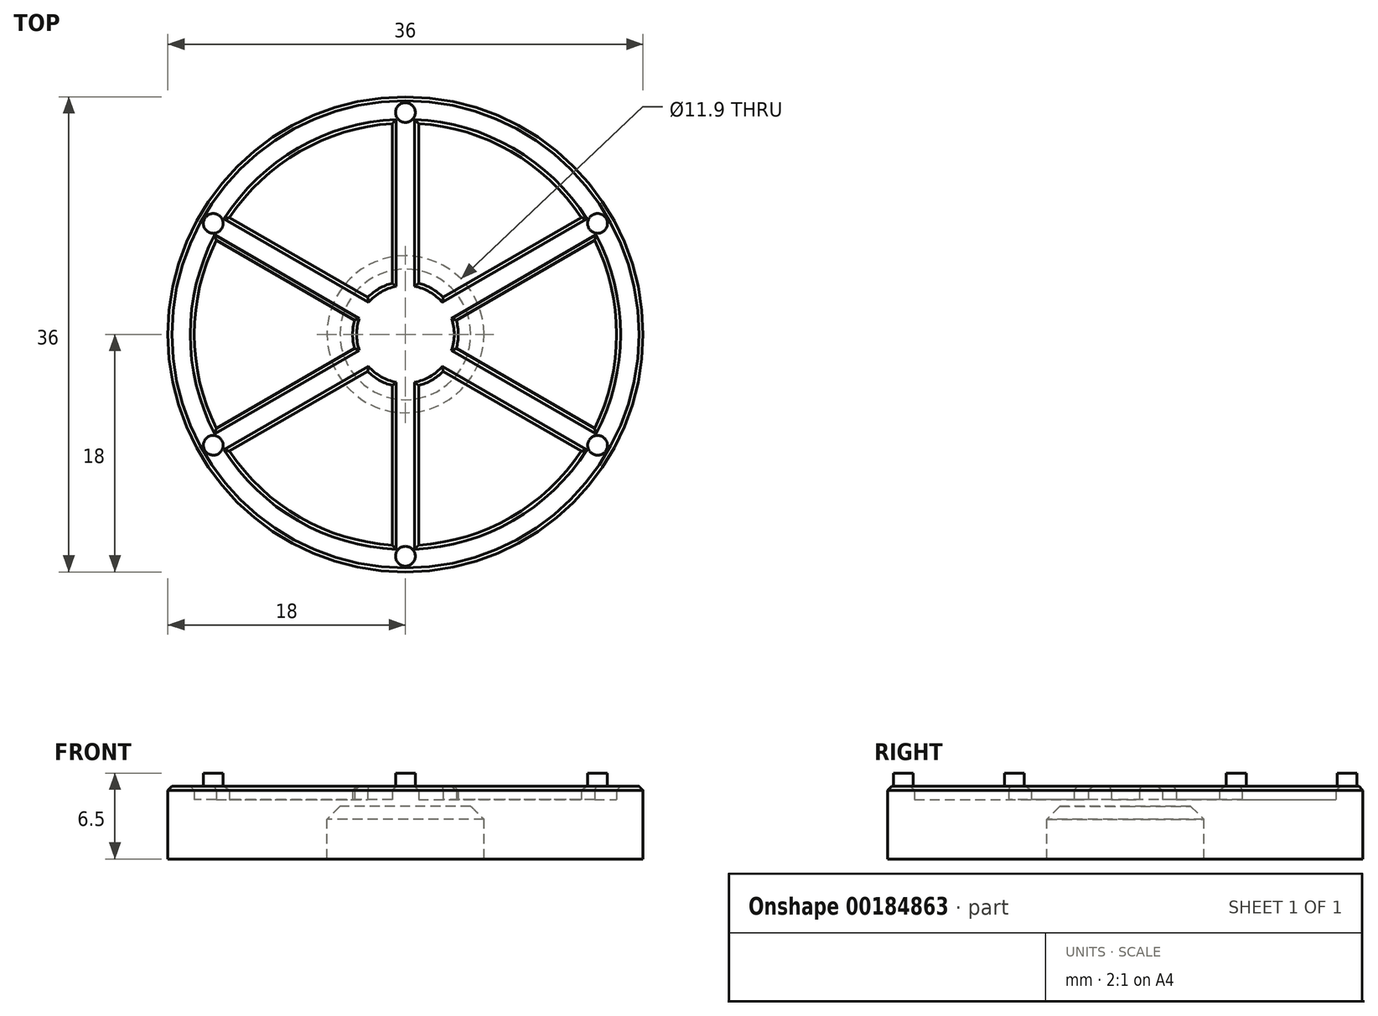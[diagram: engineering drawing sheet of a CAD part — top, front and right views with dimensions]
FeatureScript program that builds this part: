
annotation { "Feature Type Name" : "Feature", "Feature Type Description" : "" }
export const myFeature = defineFeature(function(context is Context, id is Id, definition is map)
    precondition{}
    {
        {
            var Q0;
            Q0=qCreatedBy(makeId("Top.planeOp"),FACE);
            var sketch = newSketch(context, id + "F0", { "sketchPlane" : qUnion([Q0])});
            skCircle(sketch, "E0", {"center": v(0, 0) * mm, "radius": 5.95 * mm});
            skCircle(sketch, "E1", {"center": v(0, 0) * mm, "radius": 18 * mm});
            skSolve(sketch);
        }
        {
            var Q0;
            Q0 = qSketchRegion(id + "F0", true);
            extrude(context, id + "F1", {"entities" : qUnion([Q0]), "oppositeDirection" : true, "depth" : 4 * mm});
        }
        {
            var Q0;
            Q0=qCreatedBy(makeId("Top.planeOp"),FACE);
            var sketch = newSketch(context, id + "F2", { "sketchPlane" : qUnion([Q0])});
            skCircle(sketch, "E2", {"center": v(0, 0) * mm, "radius": 18 * mm});
            skCircle(sketch, "E3", {"center": v(0, 0) * mm, "radius": 16 * mm});
            skSolve(sketch);
        }
        {
            var Q0;
            Q0 = qSketchRegion(id + "F2", true);
            extrude(context, id + "F3", {"entities" : qUnion([Q0]), "operationType" : NewBodyOperationType.ADD, "depth" : 1.5 * mm});
        }
        {
            var Q0;
            Q0=qCreatedBy(makeId("Top.planeOp"),FACE);
            var sketch = newSketch(context, id + "F4", { "sketchPlane" : qUnion([Q0])});
            skLineSegment(sketch, "E4.bottom", {"start": v(1, -16.78) * mm, "end": v(-1, -16.78) * mm});
            skLineSegment(sketch, "E4.top", {"start": v(1, 16.78) * mm, "end": v(-1, 16.78) * mm});
            skLineSegment(sketch, "E4.left", {"start": v(1, -16.78) * mm, "end": v(1, 16.78) * mm});
            skLineSegment(sketch, "E4.right", {"start": v(-1, -16.78) * mm, "end": v(-1, 16.78) * mm});
            skPoint(sketch, "E4.middle", {"position": v(0, 0) * mm});
            skCircle(sketch, "E5", {"center": v(0, 0) * mm, "radius": 4 * mm});
            skSolve(sketch);
        }
        {
            var Q0;
            Q0 = qSketchRegion(id + "F4", true);
            extrude(context, id + "F5", {"entities" : qUnion([Q0]), "depth" : 1.5 * mm});
        }
        {
            var Q0;
            {var subQ0=makeQuery(id+"F5.opExtrude","CAP_FACE",FACE,{"disambiguationData":[OSD([sQuery(id+"F4.wireOp",EDGE,"E4.bottom"),sQuery(id+"F4.wireOp",EDGE,"E4.top"),sQuery(id+"F4.wireOp",EDGE,"E4.left"),sQuery(id+"F4.wireOp",EDGE,"E4.right"),sQuery(id+"F4.wireOp",EDGE,"E5")])],"isStart":false});Q0=makeQuery(id+"F7.boolean.opBoolean","MERGE",FACE,{"derivedFrom":[makeQuery(id+"F3.opExtrude","CAP_FACE",FACE,{"disambiguationData":[OSD([sQuery(id+"F2.wireOp",EDGE,"E2"),sQuery(id+"F2.wireOp",EDGE,"E3")])],"isStart":false}),subQ0,makeQuery(id+"F7.opPattern","COPY",FACE,{"derivedFrom":subQ0,"instanceName":"1"}),makeQuery(id+"F7.opPattern","COPY",FACE,{"derivedFrom":subQ0,"instanceName":"2"})]});}
            chamfer(context, id + "F6", {"entities" : qUnion([Q0]), "width" : .3 * mm, "tangentPropagation" : true});
        }
        {
            var Q0;
            Q0=makeQuery(id+"F5.opExtrude","SWEPT_BODY",BODY,{"disambiguationData":[OSD([sQuery(id+"F4.wireOp",EDGE,"E4.bottom"),sQuery(id+"F4.wireOp",EDGE,"E4.top"),sQuery(id+"F4.wireOp",EDGE,"E4.left"),sQuery(id+"F4.wireOp",EDGE,"E4.right")])]});
            var Q1;
            Q1=makeQuery(id+"F1.opExtrude","CAP_EDGE",EDGE,{"disambiguationData":[OSD([sQuery(id+"F0.wireOp",EDGE,"E0")])],"isStart":true});
            circularPattern(context, id + "F7", {"operationType" : NewBodyOperationType.ADD, "entities" : qUnion([Q0]), "axis" : qUnion([Q1]), "angle" : 360 * degree, "instanceCount" : 3, "equalSpace" : true});
        }
        {
            var Q0;
            Q0=qCreatedBy(makeId("Top.planeOp"),FACE);
            var sketch = newSketch(context, id + "F8", { "sketchPlane" : qUnion([Q0])});
            skCircle(sketch, "E6", {"center": v(0, -16.81) * mm, "radius": 0.75 * mm});
            skSolve(sketch);
        }
        {
            var Q0;
            Q0 = qSketchRegion(id + "F8", true);
            extrude(context, id + "F9", {"entities" : qUnion([Q0]), "depth" : 2.5 * mm});
        }
        {
            var Q0;
            Q0=makeQuery(id+"F9.opExtrude","SWEPT_BODY",BODY,{"disambiguationData":[OSD([sQuery(id+"F8.wireOp",EDGE,"E6")])]});
            var Q1;
            {var subQ0=sQuery(id+"F2.wireOp",EDGE,"E2");Q1=makeQuery(id+"F6.opChamfer","BLEND_EDGE",EDGE,{"blendedFrom":[makeQuery(id+"F3.opExtrude","CAP_EDGE",EDGE,{"disambiguationData":[OSD([subQ0])],"isStart":false}),makeQuery(id+"F3.boolean.opBoolean","MERGE",FACE,{"derivedFrom":[makeQuery(id+"F1.opExtrude","SWEPT_FACE",FACE,{"disambiguationData":[OSD([sQuery(id+"F0.wireOp",EDGE,"E1")])]}),makeQuery(id+"F3.opExtrude","SWEPT_FACE",FACE,{"disambiguationData":[OSD([subQ0])]})]})],"blendedInto":[makeQuery(id+"F3.boolean.opBoolean","MERGE",FACE,{"derivedFrom":[makeQuery(id+"F1.opExtrude","SWEPT_FACE",FACE,{"disambiguationData":[OSD([sQuery(id+"F0.wireOp",EDGE,"E1")])]}),makeQuery(id+"F3.opExtrude","SWEPT_FACE",FACE,{"disambiguationData":[OSD([subQ0])]})]})]});}
            circularPattern(context, id + "F10", {"operationType" : NewBodyOperationType.ADD, "entities" : qUnion([Q0]), "axis" : qUnion([Q1]), "angle" : 360 * degree, "instanceCount" : 6, "equalSpace" : true});
        }
        {
            var Q0;
            Q0=qCreatedBy(makeId("Top.planeOp"),FACE);
            var sketch = newSketch(context, id + "F11", { "sketchPlane" : qUnion([Q0])});
            skCircle(sketch, "E7", {"center": v(0, 0) * mm, "radius": 17 * mm});
            skSolve(sketch);
        }
        {
            var Q0;
            Q0 = qSketchRegion(id + "F11", true);
            extrude(context, id + "F12", {"entities" : qUnion([Q0]), "operationType" : NewBodyOperationType.ADD, "depth" : .5 * mm});
        }
        {
            var Q0;
            {var subQ0=sQuery(id+"F4.wireOp",EDGE,"E5");var subQ1=sQuery(id+"F4.wireOp",EDGE,"E4.right");var subQ2=sQuery(id+"F4.wireOp",EDGE,"E4.left");var subQ3=sQuery(id+"F4.wireOp",EDGE,"E4.top");var subQ4=sQuery(id+"F4.wireOp",EDGE,"E4.bottom");var subQ5=makeQuery(id+"F5.opExtrude","CAP_FACE",FACE,{"disambiguationData":[OSD([subQ4,subQ3,subQ2,subQ1,subQ0])],"isStart":true});var subQ6=makeQuery(id+"F7.opPattern","COPY",FACE,{"derivedFrom":subQ5,"instanceName":"1"});var subQ7=makeQuery(id+"F7.opPattern","COPY",FACE,{"derivedFrom":subQ5,"instanceName":"2"});var subQ8=sQuery(id+"F0.wireOp",EDGE,"E0");var subQ9=makeQuery(id+"F1.opExtrude","CAP_FACE",FACE,{"disambiguationData":[OSD([subQ8,sQuery(id+"F0.wireOp",EDGE,"E1")])],"isStart":true});var subQ10=makeQuery(id+"F5.opExtrude","SWEPT_FACE",FACE,{"disambiguationData":[OSD([subQ1]),TDD([makeQuery(id+"F4.imprint","IMPRINT",EDGE,{"disambiguationData":[TD([[makeQuery(id+"F4.imprint","INTERSECT",VERTEX,{"derivedFrom":[subQ4,subQ1]}),-1.0]])],"derivedFrom":subQ1})])]});var subQ11=subQ10;var subQ12=makeQuery(id+"F7.opPattern","COPY",FACE,{"derivedFrom":subQ11,"instanceName":"1"});var subQ13=makeQuery(id+"F1.opExtrude","SWEPT_FACE",FACE,{"disambiguationData":[OSD([subQ8])]});var subQ14=makeQuery(id+"F5.opExtrude","SWEPT_FACE",FACE,{"disambiguationData":[OSD([subQ1]),TDD([makeQuery(id+"F4.imprint","IMPRINT",EDGE,{"disambiguationData":[TD([[makeQuery(id+"F4.imprint","INTERSECT",VERTEX,{"derivedFrom":[subQ3,subQ1]}),1.0]])],"derivedFrom":subQ1})])]});var subQ15=subQ14;var subQ16=makeQuery(id+"F7.opPattern","COPY",FACE,{"derivedFrom":subQ15,"instanceName":"2"});var subQ17=makeQuery(id+"F1.opExtrude","CAP_EDGE",EDGE,{"disambiguationData":[OSD([subQ8])],"isStart":true});var subQ18=makeQuery(id+"F5.opExtrude","SWEPT_FACE",FACE,{"disambiguationData":[OSD([subQ2]),TDD([makeQuery(id+"F4.imprint","IMPRINT",EDGE,{"disambiguationData":[TD([[makeQuery(id+"F4.imprint","INTERSECT",VERTEX,{"derivedFrom":[subQ3,subQ2]}),1.0]])],"derivedFrom":subQ2})])]});var subQ19=subQ18;var subQ20=makeQuery(id+"F7.opPattern","COPY",FACE,{"derivedFrom":subQ19,"instanceName":"1"});var subQ21=makeQuery(id+"F5.opExtrude","SWEPT_FACE",FACE,{"disambiguationData":[OSD([subQ2]),TDD([makeQuery(id+"F4.imprint","IMPRINT",EDGE,{"disambiguationData":[TD([[makeQuery(id+"F4.imprint","INTERSECT",VERTEX,{"derivedFrom":[subQ4,subQ2]}),-1.0]])],"derivedFrom":subQ2})])]});var subQ22=subQ21;var subQ23=makeQuery(id+"F7.opPattern","COPY",FACE,{"derivedFrom":subQ22,"instanceName":"2"});var subQ24=makeQuery(id+"F7.opPattern","COPY",FACE,{"derivedFrom":subQ11,"instanceName":"2"});var subQ25=makeQuery(id+"F7.opPattern","COPY",FACE,{"derivedFrom":subQ15,"instanceName":"1"});var subQ26=makeQuery(id+"F7.opPattern","COPY",FACE,{"derivedFrom":subQ22,"instanceName":"1"});var subQ27=makeQuery(id+"F7.opPattern","COPY",FACE,{"derivedFrom":subQ19,"instanceName":"2"});Q0=makeQuery(id+"F12.boolean.opBoolean","MERGE",EDGE,{"derivedFrom":[makeQuery(id+"F7.boolean.opBoolean","SPLIT",EDGE,{"disambiguationData":[TD([subQ13,subQ9,subQ5,subQ21,subQ10,subQ6,subQ7])],"derivedFrom":subQ17}),makeQuery(id+"F7.boolean.opBoolean","SPLIT",EDGE,{"disambiguationData":[TD([subQ13,subQ9,subQ5,subQ18,subQ14,subQ6,subQ7])],"derivedFrom":subQ17}),makeQuery(id+"F7.boolean.opBoolean","SPLIT",EDGE,{"disambiguationData":[TD([subQ13,subQ9,subQ5,subQ6,subQ26,subQ12,subQ7])],"derivedFrom":subQ17}),makeQuery(id+"F7.boolean.opBoolean","SPLIT",EDGE,{"disambiguationData":[TD([subQ13,subQ9,subQ5,subQ6,subQ20,subQ25,subQ7])],"derivedFrom":subQ17}),makeQuery(id+"F7.boolean.opBoolean","SPLIT",EDGE,{"disambiguationData":[TD([subQ13,subQ9,subQ5,subQ6,subQ7,subQ23,subQ24])],"derivedFrom":subQ17}),makeQuery(id+"F7.boolean.opBoolean","SPLIT",EDGE,{"disambiguationData":[TD([subQ13,subQ9,subQ5,subQ6,subQ7,subQ27,subQ16])],"derivedFrom":subQ17}),makeQuery(id+"F7.boolean.opBoolean","SPLIT",EDGE,{"disambiguationData":[TD([subQ13,subQ9,subQ5,subQ21,subQ6,subQ7,subQ27])],"derivedFrom":subQ17}),makeQuery(id+"F7.boolean.opBoolean","SPLIT",EDGE,{"disambiguationData":[TD([subQ13,subQ9,subQ5,subQ18,subQ6,subQ26,subQ7])],"derivedFrom":subQ17}),makeQuery(id+"F7.boolean.opBoolean","SPLIT",EDGE,{"disambiguationData":[TD([subQ13,subQ9,subQ5,subQ10,subQ6,subQ25,subQ7])],"derivedFrom":subQ17}),makeQuery(id+"F7.boolean.opBoolean","SPLIT",EDGE,{"disambiguationData":[TD([subQ13,subQ9,subQ5,subQ14,subQ6,subQ7,subQ24])],"derivedFrom":subQ17}),makeQuery(id+"F7.boolean.opBoolean","SPLIT",EDGE,{"disambiguationData":[TD([subQ13,subQ9,subQ5,subQ6,subQ20,subQ7,subQ23])],"derivedFrom":subQ17}),makeQuery(id+"F7.boolean.opBoolean","SPLIT",EDGE,{"disambiguationData":[TD([subQ13,subQ9,subQ5,subQ6,subQ12,subQ7,subQ16])],"derivedFrom":subQ17})]});}
            chamfer(context, id + "F13", {"entities" : qUnion([Q0]), "width" : 1 * mm, "tangentPropagation" : true});
        }
    });
